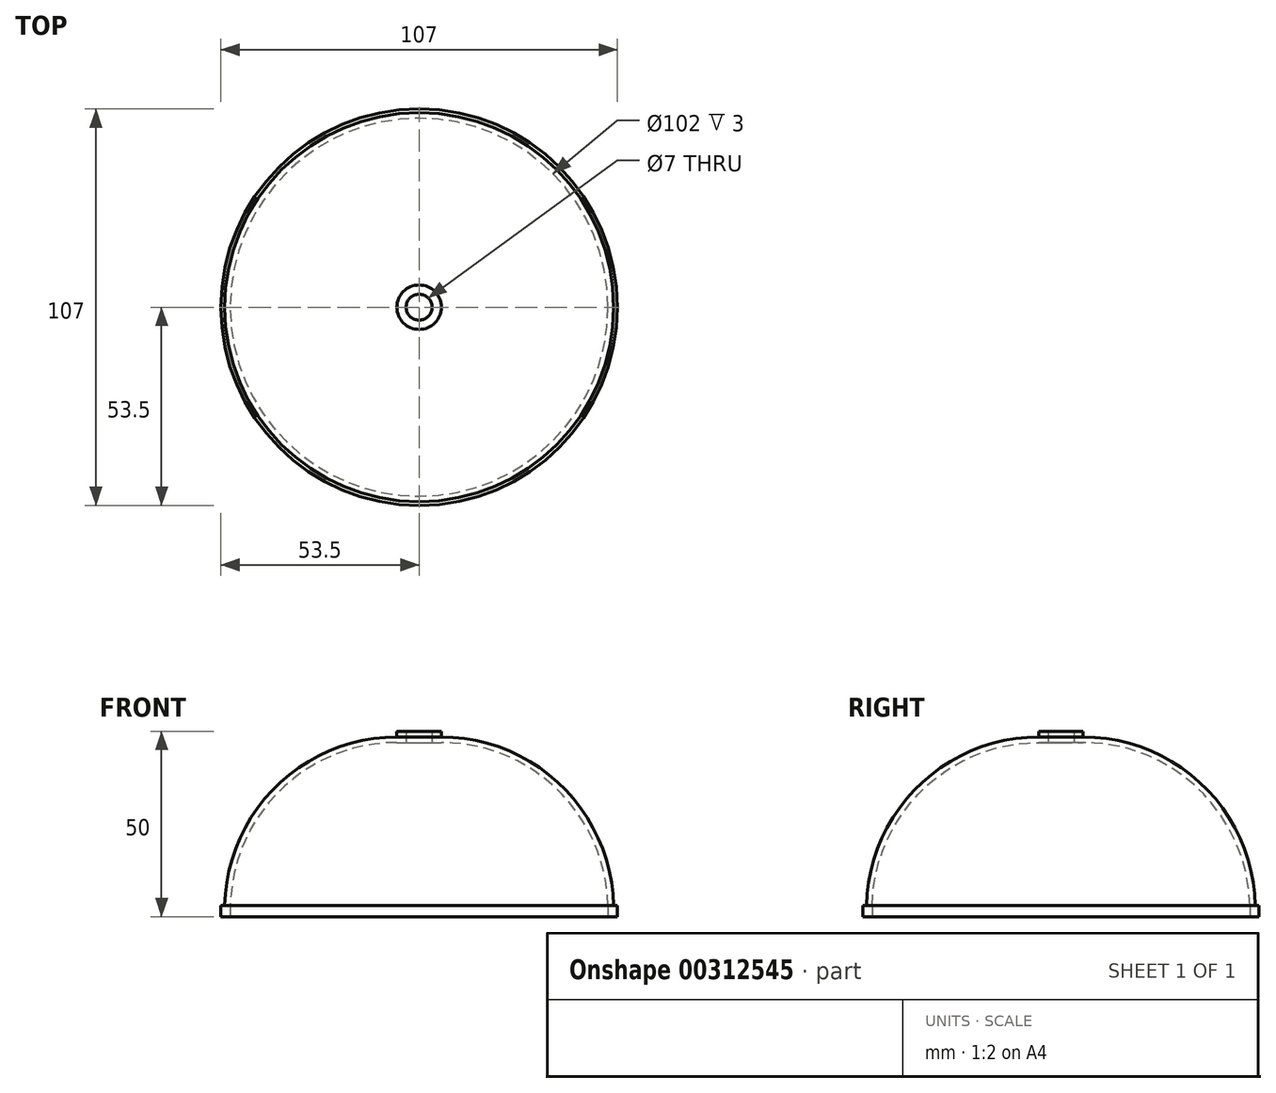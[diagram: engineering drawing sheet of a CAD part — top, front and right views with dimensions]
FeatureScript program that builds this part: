
annotation { "Feature Type Name" : "Feature", "Feature Type Description" : "" }
export const myFeature = defineFeature(function(context is Context, id is Id, definition is map)
    precondition{}
    {
        {
            var Q0;
            Q0=qCreatedBy(makeId("Right.planeOp"),FACE);
            var sketch = newSketch(context, id + "F0", { "sketchPlane" : qUnion([Q0])});
            skLineSegment(sketch, "E0", {"start": v(0, 0) * mm, "end": v(-3.5, 0) * mm, "construction": true});
            skLineSegment(sketch, "E1", {"start": v(-3.5, 0) * mm, "end": v(-3.5, 50) * mm, "construction": true});
            skLineSegment(sketch, "E2", {"start": v(-3.5, 50) * mm, "end": v(-53.5, 50) * mm, "construction": true});
            skLineSegment(sketch, "E3", {"start": v(-53.5, 50) * mm, "end": v(-53.5, 0) * mm, "construction": true});
            skLineSegment(sketch, "E4.bottom", {"start": v(-53.5, 0) * mm, "end": v(-51, 0) * mm});
            skLineSegment(sketch, "E4.top", {"start": v(-53.5, 3) * mm, "end": v(-51, 3) * mm});
            skLineSegment(sketch, "E4.left", {"start": v(-53.5, 0) * mm, "end": v(-53.5, 3) * mm});
            skLineSegment(sketch, "E4.right", {"start": v(-51, 0) * mm, "end": v(-51, 3) * mm});
            skLineSegment(sketch, "E5.bottom", {"start": v(-3.5, 50) * mm, "end": v(-6, 50) * mm});
            skLineSegment(sketch, "E5.top", {"start": v(-3.5, 47) * mm, "end": v(-6, 47) * mm});
            skLineSegment(sketch, "E5.left", {"start": v(-3.5, 50) * mm, "end": v(-3.5, 47) * mm});
            skLineSegment(sketch, "E5.right", {"start": v(-6, 50) * mm, "end": v(-6, 47) * mm});
            skArc(sketch, "E6", {"start": v(-6, 47) * mm, "mid": v(-37.47, 34.17) * mm, "end": v(-51, 3) * mm});
            skArc(sketch, "E7.0", {"start": v(-6, 48.5) * mm, "mid": v(-38.52, 35.24) * mm, "end": v(-52.5, 3.03) * mm});
            skLineSegment(sketch, "E8", {"start": v(-52.5, 3.03) * mm, "end": v(-52.5, 3) * mm});
            skLineSegment(sketch, "E9", {"start": v(0, 0) * mm, "end": v(0, 37.8) * mm, "construction": true});
            skSolve(sketch);
        }
        {
            var Q0;
            Q0=makeQuery(id+"F0.imprint","IMPRINT",FACE,{"disambiguationData":[TD([[makeQuery(id+"F0.imprint","IMPRINT",EDGE,{"derivedFrom":sQuery(id+"F0.wireOp",EDGE,"E4.bottom")}),1.0]])]});
            var Q1;
            {var subQ1=sQuery(id+"F0.wireOp",EDGE,"E5.bottom");Q1=makeQuery(id+"F0.imprint","IMPRINT",FACE,{"disambiguationData":[TD([[makeQuery(id+"F0.imprint","IMPRINT",EDGE,{"derivedFrom":subQ1}),1.0]])]});}
            var Q2;
            {var subQ1=sQuery(id+"F0.wireOp",EDGE,"E6");Q2=makeQuery(id+"F0.imprint","IMPRINT",FACE,{"disambiguationData":[TD([[makeQuery(id+"F0.imprint","IMPRINT",EDGE,{"derivedFrom":subQ1}),-1.0]])]});}
            var Q3;
            Q3=sQuery(id+"F0.wireOp",EDGE,"E9");
            revolve(context, id + "F1", {"entities" : qUnion([Q0, Q1, Q2]), "axis" : qUnion([Q3]), "revolveType" : RevolveType.FULL});
        }
    });
